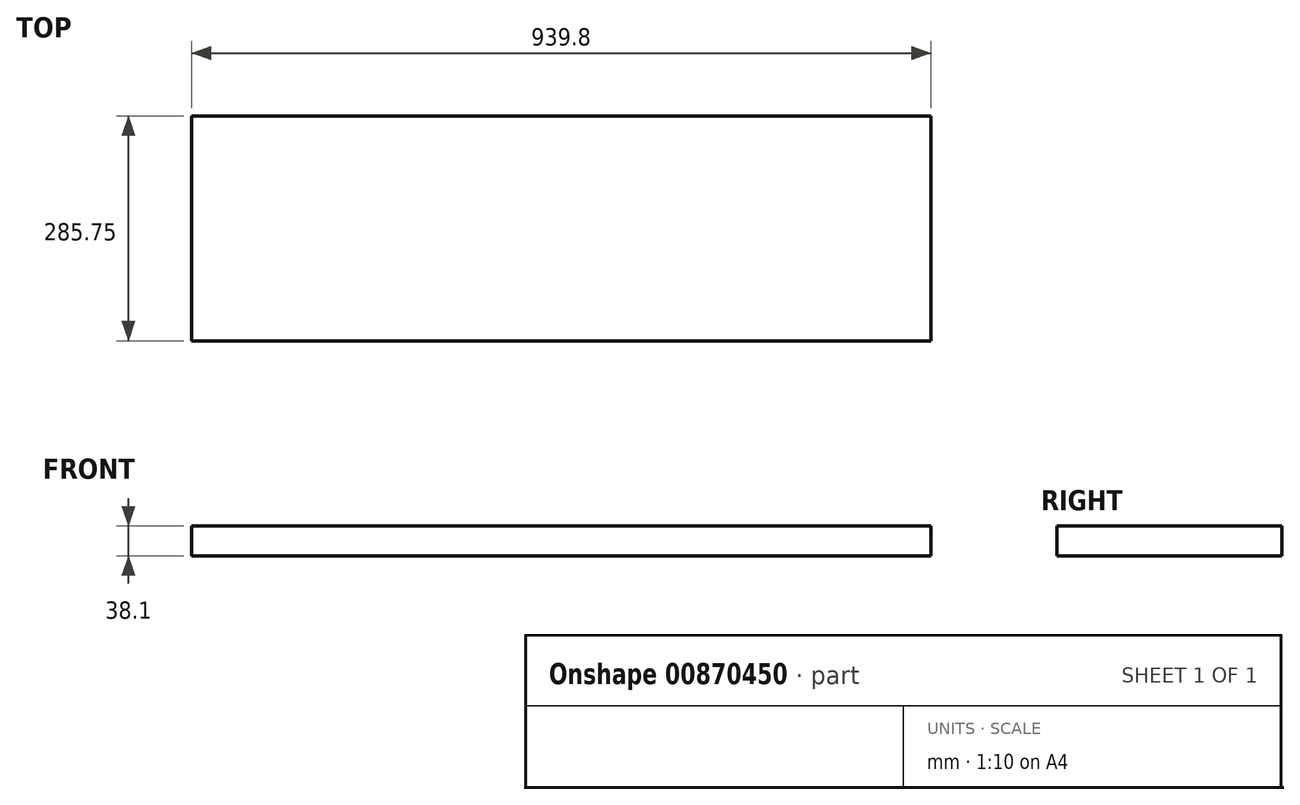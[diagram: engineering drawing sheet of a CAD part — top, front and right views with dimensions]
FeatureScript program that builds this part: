
annotation { "Feature Type Name" : "Feature", "Feature Type Description" : "" }
export const myFeature = defineFeature(function(context is Context, id is Id, definition is map)
    precondition{}
    {
        {
            var Q0;
            Q0=qCreatedBy(makeId("Right.planeOp"),FACE);
            var sketch = newSketch(context, id + "F0", { "sketchPlane" : qUnion([Q0])});
            skLineSegment(sketch, "E0.bottom", {"start": v(144.68, 19.05) * mm, "end": v(-141.07, 19.05) * mm});
            skLineSegment(sketch, "E0.top", {"start": v(144.68, -19.05) * mm, "end": v(-141.07, -19.05) * mm});
            skLineSegment(sketch, "E0.left", {"start": v(144.68, 19.05) * mm, "end": v(144.68, -19.05) * mm});
            skLineSegment(sketch, "E0.right", {"start": v(-141.07, 19.05) * mm, "end": v(-141.07, -19.05) * mm});
            skPoint(sketch, "E0.middle", {"position": v(1.8, 0) * mm});
            skSolve(sketch);
        }
        {
            var Q0;
            Q0=makeQuery(id+"F0.imprint","IMPRINT",FACE,{"disambiguationData":[TD([[makeQuery(id+"F0.imprint","IMPRINT",EDGE,{"derivedFrom":sQuery(id+"F0.wireOp",EDGE,"E0.bottom")}),1.0]])]});
            extrude(context, id + "F1", {"entities" : qUnion([Q0]), "depth" : 939.8 * mm, "offsetDistance" : 25.4 * mm});
        }
    });
